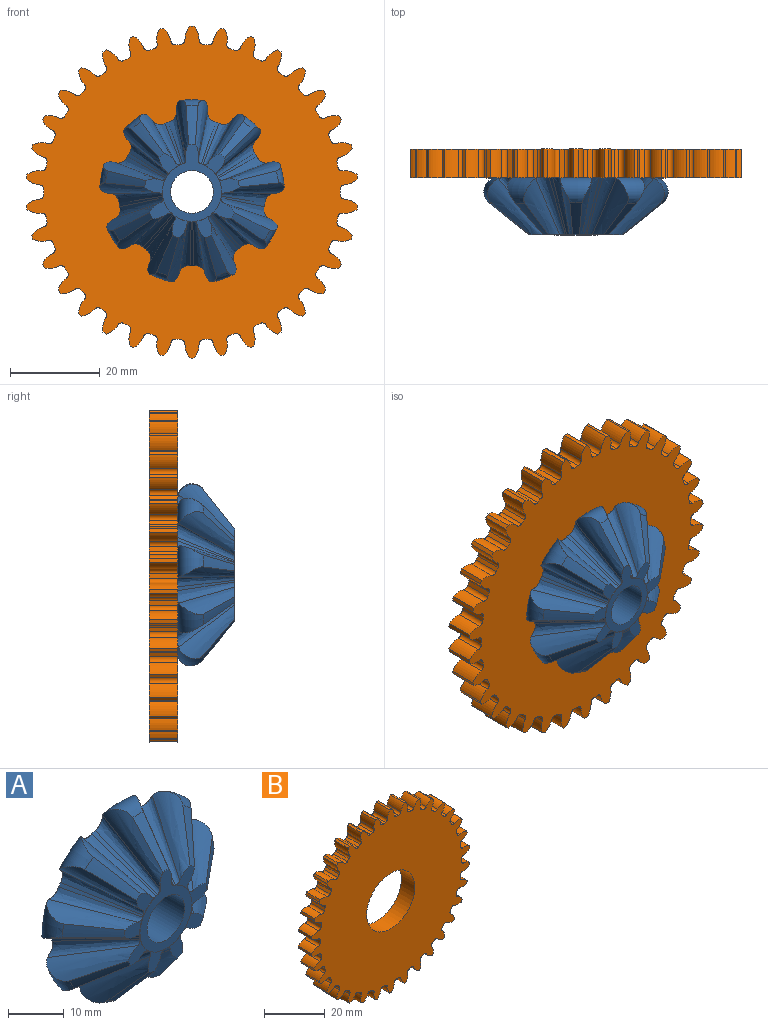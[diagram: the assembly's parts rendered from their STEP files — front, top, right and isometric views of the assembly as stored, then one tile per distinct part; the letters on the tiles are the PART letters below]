
ASSEMBLY  parts=2 mates=1
PART A: 80 faces, bbox 52.7x12.8x51.3 mm
  f0: cylinder r=6.59mm len=13.18mm, axis (0,1,0), area 3.7mm2, adj f1,f5,f6,f8,f14,f16,f17,f24
  f1: plane 17.18x13.18mm, normal (0,-1,0), area 76mm2, adj f0,f2,f3,f4,f5,f6,f79
  f2: cylinder r=4.44mm len=3.2mm, axis (0,1,0), area 0.3mm2, adj f1,f3,f6,f10
  f3: cylinder r=10.59mm len=1.48mm, axis (0,1,0), area 0.1mm2, adj f1,f2,f4,f11
  f4: cylinder r=4.44mm len=3.2mm, axis (0,1,0), area 0.3mm2, adj f1,f3,f5,f12
  f5: cylinder r=1mm len=1.11mm, axis (0,1,0), area 0.1mm2, adj f0,f1,f4,f13
  f6: cylinder r=1mm len=1.11mm, axis (0,1,0), area 0.1mm2, adj f0,f1,f2,f9
  f7: plane 34.79x34.62mm, normal (0,1,0), area 845.9mm2, adj f8,f9,f13,f14,f15,f17,f18,f22
  f8: cone r=6.59mm half-angle=37.9deg, axis (0,1,0), area 9.7mm2, adj f0,f7,f9,f22
  f9: bspline ~12.65x12.14mm, area 36.5mm2, adj f6,f7,f8,f10,f15
  f10: bspline ~18.78x12.44mm, area 59.6mm2, adj f2,f9,f11,f15
  f11: cone r=10.59mm half-angle=51.5deg, axis (0,1,0), area 23.5mm2, adj f3,f10,f12,f15
  f12: bspline ~18.78x12.44mm, area 59.6mm2, adj f4,f11,f13,f15
  f13: bspline ~12.65x12.14mm, area 36.5mm2, adj f5,f7,f12,f14,f15
  f14: cone r=6.59mm half-angle=37.9deg, axis (0,1,0), area 9.7mm2, adj f0,f7,f13,f73
  f15: torus R=17.39mm, axis (0,-1,0), area 42.8mm2, adj f7,f9,f10,f11,f12,f13
  f16: plane 5.12x4.94mm, normal (0,-1,0), area 10.8mm2, adj f0,f18,f19,f20,f21,f22
  f17: cone r=6.59mm half-angle=37.9deg, axis (0,1,0), area 9.7mm2, adj f0,f7,f18,f30
  f18: bspline ~12.65x9.08mm, area 36.5mm2, adj f7,f16,f17,f19,f23
  f19: bspline ~14.13x12.44mm, area 59.6mm2, adj f16,f18,f20,f23
  f20: cone r=10.59mm half-angle=51.5deg, axis (0,1,0), area 23.5mm2, adj f16,f19,f21,f23
  f21: bspline ~14.87x12.65mm, area 59.6mm2, adj f16,f20,f22,f23
  f22: bspline ~12.65x10.31mm, area 36.5mm2, adj f7,f8,f16,f21,f23
  f23: torus R=17.39mm, axis (0,-1,0), area 42.8mm2, adj f7,f18,f19,f20,f21,f22
  f24: plane 4.74x4.12mm, normal (0,-1,0), area 10.8mm2, adj f0,f26,f27,f28,f29,f30
  f25: cone r=6.59mm half-angle=37.9deg, axis (0,1,0), area 9.7mm2, adj f0,f7,f26,f38
  f26: bspline ~12.65x12.21mm, area 36.5mm2, adj f7,f24,f25,f27,f31
  f27: bspline ~18.84x12.65mm, area 59.6mm2, adj f24,f26,f28,f31
  f28: cone r=10.59mm half-angle=51.5deg, axis (0,1,0), area 23.5mm2, adj f24,f27,f29,f31
  f29: bspline ~18.43x12.44mm, area 59.6mm2, adj f24,f28,f30,f31
  f30: bspline ~12.65x11.71mm, area 36.5mm2, adj f7,f17,f24,f29,f31
  f31: torus R=17.39mm, axis (0,-1,0), area 42.8mm2, adj f7,f26,f27,f28,f29,f30
  f32: plane 5.15x4.62mm, normal (0,-1,0), area 10.8mm2, adj f0,f34,f35,f36,f37,f38
  f33: cone r=6.59mm half-angle=37.9deg, axis (0,1,0), area 9.7mm2, adj f0,f7,f34,f46
  f34: bspline ~12.65x9.79mm, area 36.5mm2, adj f7,f32,f33,f35,f39
  f35: bspline ~16.06x12.44mm, area 59.6mm2, adj f32,f34,f36,f39
  f36: cone r=10.59mm half-angle=51.5deg, axis (0,1,0), area 23.5mm2, adj f32,f35,f37,f39
  f37: bspline ~16.71x12.65mm, area 59.6mm2, adj f32,f36,f38,f39
  f38: bspline ~12.65x11.27mm, area 36.5mm2, adj f7,f25,f32,f37,f39
  f39: torus R=17.39mm, axis (0,-1,0), area 42.8mm2, adj f7,f34,f35,f36,f37,f38
  f40: plane 5.02x4.27mm, normal (0,-1,0), area 10.8mm2, adj f0,f42,f43,f44,f45,f46
  f41: cone r=6.59mm half-angle=37.9deg, axis (0,1,0), area 9.7mm2, adj f0,f7,f42,f54
  f42: bspline ~12.65x11.91mm, area 36.5mm2, adj f7,f40,f41,f43,f47
  f43: bspline ~17.79x12.44mm, area 59.6mm2, adj f40,f42,f44,f47
  f44: cone r=10.59mm half-angle=51.5deg, axis (0,1,0), area 23.5mm2, adj f40,f43,f45,f47
  f45: bspline ~17.76x12.65mm, area 59.6mm2, adj f40,f44,f46,f47
  f46: bspline ~12.65x10.91mm, area 36.5mm2, adj f7,f33,f40,f45,f47
  f47: torus R=17.39mm, axis (0,-1,0), area 42.8mm2, adj f7,f42,f43,f44,f45,f46
  f48: plane 5.02x4.27mm, normal (0,-1,0), area 10.8mm2, adj f0,f50,f51,f52,f53,f54
  f49: cone r=6.59mm half-angle=37.9deg, axis (0,1,0), area 9.7mm2, adj f0,f7,f50,f62
  f50: bspline ~12.65x10.91mm, area 36.5mm2, adj f7,f48,f49,f51,f55
  f51: bspline ~17.76x12.65mm, area 59.6mm2, adj f48,f50,f52,f55
  f52: cone r=10.59mm half-angle=51.5deg, axis (0,1,0), area 23.5mm2, adj f48,f51,f53,f55
  f53: bspline ~17.79x12.44mm, area 59.6mm2, adj f48,f52,f54,f55
  f54: bspline ~12.65x11.91mm, area 36.5mm2, adj f7,f41,f48,f53,f55
  f55: torus R=17.39mm, axis (0,-1,0), area 42.8mm2, adj f7,f50,f51,f52,f53,f54
  f56: plane 5.15x4.62mm, normal (0,-1,0), area 10.8mm2, adj f0,f58,f59,f60,f61,f62
  f57: cone r=6.59mm half-angle=37.9deg, axis (0,1,0), area 9.7mm2, adj f0,f7,f58,f70
  f58: bspline ~12.65x11.27mm, area 36.5mm2, adj f7,f56,f57,f59,f63
  f59: bspline ~16.71x12.65mm, area 59.6mm2, adj f56,f58,f60,f63
  f60: cone r=10.59mm half-angle=51.5deg, axis (0,1,0), area 23.5mm2, adj f56,f59,f61,f63
  f61: bspline ~16.06x12.44mm, area 59.6mm2, adj f56,f60,f62,f63
  f62: bspline ~12.65x9.79mm, area 36.5mm2, adj f7,f49,f56,f61,f63
  f63: torus R=17.39mm, axis (0,-1,0), area 42.8mm2, adj f7,f58,f59,f60,f61,f62
  f64: plane 4.74x4.12mm, normal (0,-1,0), area 10.8mm2, adj f0,f66,f67,f68,f69,f70
  f65: cone r=6.59mm half-angle=37.9deg, axis (0,1,0), area 9.7mm2, adj f0,f7,f66,f77
  f66: bspline ~12.65x11.71mm, area 36.5mm2, adj f7,f64,f65,f67,f71
  f67: bspline ~18.43x12.44mm, area 59.6mm2, adj f64,f66,f68,f71
  f68: cone r=10.59mm half-angle=51.5deg, axis (0,1,0), area 23.5mm2, adj f64,f67,f69,f71
  f69: bspline ~18.84x12.65mm, area 59.6mm2, adj f64,f68,f70,f71
  f70: bspline ~12.65x12.21mm, area 36.5mm2, adj f7,f57,f64,f69,f71
  f71: torus R=17.39mm, axis (0,-1,0), area 42.8mm2, adj f7,f66,f67,f68,f69,f70
  f72: plane 5.12x4.94mm, normal (0,-1,0), area 10.8mm2, adj f0,f73,f74,f75,f76,f77
  f73: bspline ~12.65x10.31mm, area 36.5mm2, adj f7,f14,f72,f74,f78
  f74: bspline ~14.87x12.65mm, area 59.6mm2, adj f72,f73,f75,f78
  f75: cone r=10.59mm half-angle=51.5deg, axis (0,1,0), area 23.5mm2, adj f72,f74,f76,f78
  f76: bspline ~14.13x12.44mm, area 59.6mm2, adj f72,f75,f77,f78
  f77: bspline ~12.65x9.08mm, area 36.5mm2, adj f7,f65,f72,f76,f78
  f78: torus R=17.39mm, axis (0,-1,0), area 42.8mm2, adj f7,f73,f74,f75,f76,f77
  f79: cylinder r=4.76mm len=12.75mm, axis (0,-1,0), area 381.5mm2, adj f1,f7
PART B: 207 faces, bbox 73.8x6.4x74 mm
  f0: cylinder r=33mm len=6.35mm, axis (0,1,0), area 7mm2, adj f34,f35,f40,f204
  f1: cylinder r=33mm len=6.35mm, axis (0,1,0), area 7mm2, adj f34,f35,f199,f205
  f2: cylinder r=33mm len=6.35mm, axis (0,1,0), area 7mm2, adj f34,f35,f194,f200
  f3: cylinder r=33mm len=6.35mm, axis (0,1,0), area 7mm2, adj f34,f35,f189,f195
  f4: cylinder r=33mm len=6.35mm, axis (0,1,0), area 7mm2, adj f34,f35,f184,f190
  f5: cylinder r=33mm len=6.35mm, axis (0,1,0), area 7mm2, adj f34,f35,f179,f185
  f6: cylinder r=33mm len=6.35mm, axis (0,1,0), area 7mm2, adj f34,f35,f174,f180
  f7: cylinder r=33mm len=6.35mm, axis (0,1,0), area 7mm2, adj f34,f35,f169,f175
  f8: cylinder r=33mm len=6.35mm, axis (0,1,0), area 7mm2, adj f34,f35,f164,f170
  f9: cylinder r=33mm len=6.35mm, axis (0,1,0), area 7mm2, adj f34,f35,f159,f165
  f10: cylinder r=33mm len=6.35mm, axis (0,1,0), area 7mm2, adj f34,f35,f154,f160
  f11: cylinder r=33mm len=6.35mm, axis (0,1,0), area 7mm2, adj f34,f35,f149,f155
  f12: cylinder r=33mm len=6.35mm, axis (0,1,0), area 7mm2, adj f34,f35,f144,f150
  f13: cylinder r=33mm len=6.35mm, axis (0,1,0), area 7mm2, adj f34,f35,f139,f145
  f14: cylinder r=33mm len=6.35mm, axis (0,1,0), area 7mm2, adj f34,f35,f134,f140
  f15: cylinder r=33mm len=6.35mm, axis (0,1,0), area 7mm2, adj f34,f35,f129,f135
  f16: cylinder r=33mm len=6.35mm, axis (0,1,0), area 7mm2, adj f34,f35,f124,f130
  f17: cylinder r=33mm len=6.35mm, axis (0,1,0), area 7mm2, adj f34,f35,f119,f125
  f18: cylinder r=33mm len=6.35mm, axis (0,1,0), area 7mm2, adj f34,f35,f114,f120
  f19: cylinder r=33mm len=6.35mm, axis (0,1,0), area 7mm2, adj f34,f35,f109,f115
  f20: cylinder r=33mm len=6.35mm, axis (0,1,0), area 7mm2, adj f34,f35,f104,f110
  f21: cylinder r=33mm len=6.35mm, axis (0,1,0), area 7mm2, adj f34,f35,f99,f105
  f22: cylinder r=33mm len=6.35mm, axis (0,1,0), area 7mm2, adj f34,f35,f94,f100
  f23: cylinder r=33mm len=6.35mm, axis (0,1,0), area 7mm2, adj f34,f35,f89,f95
  f24: cylinder r=33mm len=6.35mm, axis (0,1,0), area 7mm2, adj f34,f35,f84,f90
  f25: cylinder r=33mm len=6.35mm, axis (0,1,0), area 7mm2, adj f34,f35,f79,f85
  f26: cylinder r=33mm len=6.35mm, axis (0,1,0), area 7mm2, adj f34,f35,f74,f80
  f27: cylinder r=33mm len=6.35mm, axis (0,1,0), area 7mm2, adj f34,f35,f69,f75
  f28: cylinder r=33mm len=6.35mm, axis (0,1,0), area 7mm2, adj f34,f35,f64,f70
  f29: cylinder r=33mm len=6.35mm, axis (0,1,0), area 7mm2, adj f34,f35,f59,f65
  f30: cylinder r=33mm len=6.35mm, axis (0,1,0), area 7mm2, adj f34,f35,f54,f60
  f31: cylinder r=33mm len=6.35mm, axis (0,1,0), area 7mm2, adj f34,f35,f49,f55
  f32: cylinder r=33mm len=6.35mm, axis (0,1,0), area 7mm2, adj f34,f35,f44,f50
  f33: cylinder r=33mm len=6.35mm, axis (0,1,0), area 7mm2, adj f34,f35,f39,f45
  f34: plane 74x73.76mm, normal (0,-1,0), area 3393.5mm2, adj f0,f1,f2,f3,f4,f5,f6,f7
  f35: plane 74x73.76mm, normal (0,1,0), area 3393.5mm2, adj f0,f1,f2,f3,f4,f5,f6,f7
  f36: cylinder r=4.53mm len=6.35mm, axis (0,1,0), area 21.2mm2, adj f34,f35,f37,f40
  f37: cylinder r=37mm len=6.35mm, axis (0,1,0), area 5.8mm2, adj f34,f35,f36,f38
  f38: cylinder r=4.53mm len=6.35mm, axis (0,1,0), area 21.2mm2, adj f34,f35,f37,f39
  f39: cylinder r=1mm len=6.35mm, axis (0,1,0), area 9.6mm2, adj f33,f34,f35,f38
  f40: cylinder r=1mm len=6.35mm, axis (0,1,0), area 9.6mm2, adj f0,f34,f35,f36
  f41: cylinder r=4.53mm len=6.35mm, axis (0,1,0), area 21.2mm2, adj f34,f35,f42,f45
  f42: cylinder r=37mm len=6.35mm, axis (0,1,0), area 5.8mm2, adj f34,f35,f41,f43
  f43: cylinder r=4.53mm len=6.35mm, axis (0,1,0), area 21.2mm2, adj f34,f35,f42,f44
  f44: cylinder r=1mm len=6.35mm, axis (0,1,0), area 9.6mm2, adj f32,f34,f35,f43
  f45: cylinder r=1mm len=6.35mm, axis (0,1,0), area 9.6mm2, adj f33,f34,f35,f41
  f46: cylinder r=4.53mm len=6.35mm, axis (0,1,0), area 21.2mm2, adj f34,f35,f47,f50
  f47: cylinder r=37mm len=6.35mm, axis (0,1,0), area 5.8mm2, adj f34,f35,f46,f48
  f48: cylinder r=4.53mm len=6.35mm, axis (0,1,0), area 21.2mm2, adj f34,f35,f47,f49
  f49: cylinder r=1mm len=6.35mm, axis (0,1,0), area 9.6mm2, adj f31,f34,f35,f48
  f50: cylinder r=1mm len=6.35mm, axis (0,1,0), area 9.6mm2, adj f32,f34,f35,f46
  f51: cylinder r=4.53mm len=6.35mm, axis (0,1,0), area 21.2mm2, adj f34,f35,f52,f55
  f52: cylinder r=37mm len=6.35mm, axis (0,1,0), area 5.8mm2, adj f34,f35,f51,f53
  f53: cylinder r=4.53mm len=6.35mm, axis (0,1,0), area 21.2mm2, adj f34,f35,f52,f54
  f54: cylinder r=1mm len=6.35mm, axis (0,1,0), area 9.6mm2, adj f30,f34,f35,f53
  f55: cylinder r=1mm len=6.35mm, axis (0,1,0), area 9.6mm2, adj f31,f34,f35,f51
  f56: cylinder r=4.53mm len=6.35mm, axis (0,1,0), area 21.2mm2, adj f34,f35,f57,f60
  f57: cylinder r=37mm len=6.35mm, axis (0,1,0), area 5.8mm2, adj f34,f35,f56,f58
  f58: cylinder r=4.53mm len=6.35mm, axis (0,1,0), area 21.2mm2, adj f34,f35,f57,f59
  f59: cylinder r=1mm len=6.35mm, axis (0,1,0), area 9.6mm2, adj f29,f34,f35,f58
  f60: cylinder r=1mm len=6.35mm, axis (0,1,0), area 9.6mm2, adj f30,f34,f35,f56
  f61: cylinder r=4.53mm len=6.35mm, axis (0,1,0), area 21.2mm2, adj f34,f35,f62,f65
  f62: cylinder r=37mm len=6.35mm, axis (0,1,0), area 5.8mm2, adj f34,f35,f61,f63
  f63: cylinder r=4.53mm len=6.35mm, axis (0,1,0), area 21.2mm2, adj f34,f35,f62,f64
  f64: cylinder r=1mm len=6.35mm, axis (0,1,0), area 9.6mm2, adj f28,f34,f35,f63
  f65: cylinder r=1mm len=6.35mm, axis (0,1,0), area 9.6mm2, adj f29,f34,f35,f61
  f66: cylinder r=4.53mm len=6.35mm, axis (0,1,0), area 21.2mm2, adj f34,f35,f67,f70
  f67: cylinder r=37mm len=6.35mm, axis (0,1,0), area 5.8mm2, adj f34,f35,f66,f68
  f68: cylinder r=4.53mm len=6.35mm, axis (0,1,0), area 21.2mm2, adj f34,f35,f67,f69
  f69: cylinder r=1mm len=6.35mm, axis (0,1,0), area 9.6mm2, adj f27,f34,f35,f68
  f70: cylinder r=1mm len=6.35mm, axis (0,1,0), area 9.6mm2, adj f28,f34,f35,f66
  f71: cylinder r=4.53mm len=6.35mm, axis (0,1,0), area 21.2mm2, adj f34,f35,f72,f75
  f72: cylinder r=37mm len=6.35mm, axis (0,1,0), area 5.8mm2, adj f34,f35,f71,f73
  f73: cylinder r=4.53mm len=6.35mm, axis (0,1,0), area 21.2mm2, adj f34,f35,f72,f74
  f74: cylinder r=1mm len=6.35mm, axis (0,1,0), area 9.6mm2, adj f26,f34,f35,f73
  f75: cylinder r=1mm len=6.35mm, axis (0,1,0), area 9.6mm2, adj f27,f34,f35,f71
  f76: cylinder r=4.53mm len=6.35mm, axis (0,1,0), area 21.2mm2, adj f34,f35,f77,f80
  f77: cylinder r=37mm len=6.35mm, axis (0,1,0), area 5.8mm2, adj f34,f35,f76,f78
  f78: cylinder r=4.53mm len=6.35mm, axis (0,1,0), area 21.2mm2, adj f34,f35,f77,f79
  f79: cylinder r=1mm len=6.35mm, axis (0,1,0), area 9.6mm2, adj f25,f34,f35,f78
  f80: cylinder r=1mm len=6.35mm, axis (0,1,0), area 9.6mm2, adj f26,f34,f35,f76
  f81: cylinder r=4.53mm len=6.35mm, axis (0,1,0), area 21.2mm2, adj f34,f35,f82,f85
  f82: cylinder r=37mm len=6.35mm, axis (0,1,0), area 5.8mm2, adj f34,f35,f81,f83
  f83: cylinder r=4.53mm len=6.35mm, axis (0,1,0), area 21.2mm2, adj f34,f35,f82,f84
  f84: cylinder r=1mm len=6.35mm, axis (0,1,0), area 9.6mm2, adj f24,f34,f35,f83
  f85: cylinder r=1mm len=6.35mm, axis (0,1,0), area 9.6mm2, adj f25,f34,f35,f81
  f86: cylinder r=4.53mm len=6.35mm, axis (0,1,0), area 21.2mm2, adj f34,f35,f87,f90
  f87: cylinder r=37mm len=6.35mm, axis (0,1,0), area 5.8mm2, adj f34,f35,f86,f88
  f88: cylinder r=4.53mm len=6.35mm, axis (0,1,0), area 21.2mm2, adj f34,f35,f87,f89
  f89: cylinder r=1mm len=6.35mm, axis (0,1,0), area 9.6mm2, adj f23,f34,f35,f88
  f90: cylinder r=1mm len=6.35mm, axis (0,1,0), area 9.6mm2, adj f24,f34,f35,f86
  f91: cylinder r=4.53mm len=6.35mm, axis (0,1,0), area 21.2mm2, adj f34,f35,f92,f95
  f92: cylinder r=37mm len=6.35mm, axis (0,1,0), area 5.8mm2, adj f34,f35,f91,f93
  f93: cylinder r=4.53mm len=6.35mm, axis (0,1,0), area 21.2mm2, adj f34,f35,f92,f94
  f94: cylinder r=1mm len=6.35mm, axis (0,1,0), area 9.6mm2, adj f22,f34,f35,f93
  f95: cylinder r=1mm len=6.35mm, axis (0,1,0), area 9.6mm2, adj f23,f34,f35,f91
  f96: cylinder r=4.53mm len=6.35mm, axis (0,1,0), area 21.2mm2, adj f34,f35,f97,f100
  f97: cylinder r=37mm len=6.35mm, axis (0,1,0), area 5.8mm2, adj f34,f35,f96,f98
  f98: cylinder r=4.53mm len=6.35mm, axis (0,1,0), area 21.2mm2, adj f34,f35,f97,f99
  f99: cylinder r=1mm len=6.35mm, axis (0,1,0), area 9.6mm2, adj f21,f34,f35,f98
  f100: cylinder r=1mm len=6.35mm, axis (0,1,0), area 9.6mm2, adj f22,f34,f35,f96
  f101: cylinder r=4.53mm len=6.35mm, axis (0,1,0), area 21.2mm2, adj f34,f35,f102,f105
  f102: cylinder r=37mm len=6.35mm, axis (0,1,0), area 5.8mm2, adj f34,f35,f101,f103
  f103: cylinder r=4.53mm len=6.35mm, axis (0,1,0), area 21.2mm2, adj f34,f35,f102,f104
  f104: cylinder r=1mm len=6.35mm, axis (0,1,0), area 9.6mm2, adj f20,f34,f35,f103
  f105: cylinder r=1mm len=6.35mm, axis (0,1,0), area 9.6mm2, adj f21,f34,f35,f101
  f106: cylinder r=4.53mm len=6.35mm, axis (0,1,0), area 21.2mm2, adj f34,f35,f107,f110
  f107: cylinder r=37mm len=6.35mm, axis (0,1,0), area 5.8mm2, adj f34,f35,f106,f108
  f108: cylinder r=4.53mm len=6.35mm, axis (0,1,0), area 21.2mm2, adj f34,f35,f107,f109
  f109: cylinder r=1mm len=6.35mm, axis (0,1,0), area 9.6mm2, adj f19,f34,f35,f108
  f110: cylinder r=1mm len=6.35mm, axis (0,1,0), area 9.6mm2, adj f20,f34,f35,f106
  f111: cylinder r=4.53mm len=6.35mm, axis (0,1,0), area 21.2mm2, adj f34,f35,f112,f115
  f112: cylinder r=37mm len=6.35mm, axis (0,1,0), area 5.8mm2, adj f34,f35,f111,f113
  f113: cylinder r=4.53mm len=6.35mm, axis (0,1,0), area 21.2mm2, adj f34,f35,f112,f114
  f114: cylinder r=1mm len=6.35mm, axis (0,1,0), area 9.6mm2, adj f18,f34,f35,f113
  f115: cylinder r=1mm len=6.35mm, axis (0,1,0), area 9.6mm2, adj f19,f34,f35,f111
  f116: cylinder r=4.53mm len=6.35mm, axis (0,1,0), area 21.2mm2, adj f34,f35,f117,f120
  f117: cylinder r=37mm len=6.35mm, axis (0,1,0), area 5.8mm2, adj f34,f35,f116,f118
  f118: cylinder r=4.53mm len=6.35mm, axis (0,1,0), area 21.2mm2, adj f34,f35,f117,f119
  f119: cylinder r=1mm len=6.35mm, axis (0,1,0), area 9.6mm2, adj f17,f34,f35,f118
  f120: cylinder r=1mm len=6.35mm, axis (0,1,0), area 9.6mm2, adj f18,f34,f35,f116
  f121: cylinder r=4.53mm len=6.35mm, axis (0,1,0), area 21.2mm2, adj f34,f35,f122,f125
  f122: cylinder r=37mm len=6.35mm, axis (0,1,0), area 5.8mm2, adj f34,f35,f121,f123
  f123: cylinder r=4.53mm len=6.35mm, axis (0,1,0), area 21.2mm2, adj f34,f35,f122,f124
  f124: cylinder r=1mm len=6.35mm, axis (0,1,0), area 9.6mm2, adj f16,f34,f35,f123
  f125: cylinder r=1mm len=6.35mm, axis (0,1,0), area 9.6mm2, adj f17,f34,f35,f121
  f126: cylinder r=4.53mm len=6.35mm, axis (0,1,0), area 21.2mm2, adj f34,f35,f127,f130
  f127: cylinder r=37mm len=6.35mm, axis (0,1,0), area 5.8mm2, adj f34,f35,f126,f128
  f128: cylinder r=4.53mm len=6.35mm, axis (0,1,0), area 21.2mm2, adj f34,f35,f127,f129
  f129: cylinder r=1mm len=6.35mm, axis (0,1,0), area 9.6mm2, adj f15,f34,f35,f128
  f130: cylinder r=1mm len=6.35mm, axis (0,1,0), area 9.6mm2, adj f16,f34,f35,f126
  f131: cylinder r=4.53mm len=6.35mm, axis (0,1,0), area 21.2mm2, adj f34,f35,f132,f135
  f132: cylinder r=37mm len=6.35mm, axis (0,1,0), area 5.8mm2, adj f34,f35,f131,f133
  f133: cylinder r=4.53mm len=6.35mm, axis (0,1,0), area 21.2mm2, adj f34,f35,f132,f134
  f134: cylinder r=1mm len=6.35mm, axis (0,1,0), area 9.6mm2, adj f14,f34,f35,f133
  f135: cylinder r=1mm len=6.35mm, axis (0,1,0), area 9.6mm2, adj f15,f34,f35,f131
  f136: cylinder r=4.53mm len=6.35mm, axis (0,1,0), area 21.2mm2, adj f34,f35,f137,f140
  f137: cylinder r=37mm len=6.35mm, axis (0,1,0), area 5.8mm2, adj f34,f35,f136,f138
  f138: cylinder r=4.53mm len=6.35mm, axis (0,1,0), area 21.2mm2, adj f34,f35,f137,f139
  f139: cylinder r=1mm len=6.35mm, axis (0,1,0), area 9.6mm2, adj f13,f34,f35,f138
  f140: cylinder r=1mm len=6.35mm, axis (0,1,0), area 9.6mm2, adj f14,f34,f35,f136
  f141: cylinder r=4.53mm len=6.35mm, axis (0,1,0), area 21.2mm2, adj f34,f35,f142,f145
  f142: cylinder r=37mm len=6.35mm, axis (0,1,0), area 5.8mm2, adj f34,f35,f141,f143
  f143: cylinder r=4.53mm len=6.35mm, axis (0,1,0), area 21.2mm2, adj f34,f35,f142,f144
  f144: cylinder r=1mm len=6.35mm, axis (0,1,0), area 9.6mm2, adj f12,f34,f35,f143
  f145: cylinder r=1mm len=6.35mm, axis (0,1,0), area 9.6mm2, adj f13,f34,f35,f141
  f146: cylinder r=4.53mm len=6.35mm, axis (0,1,0), area 21.2mm2, adj f34,f35,f147,f150
  f147: cylinder r=37mm len=6.35mm, axis (0,1,0), area 5.8mm2, adj f34,f35,f146,f148
  f148: cylinder r=4.53mm len=6.35mm, axis (0,1,0), area 21.2mm2, adj f34,f35,f147,f149
  f149: cylinder r=1mm len=6.35mm, axis (0,1,0), area 9.6mm2, adj f11,f34,f35,f148
  f150: cylinder r=1mm len=6.35mm, axis (0,1,0), area 9.6mm2, adj f12,f34,f35,f146
  f151: cylinder r=4.53mm len=6.35mm, axis (0,1,0), area 21.2mm2, adj f34,f35,f152,f155
  f152: cylinder r=37mm len=6.35mm, axis (0,1,0), area 5.8mm2, adj f34,f35,f151,f153
  f153: cylinder r=4.53mm len=6.35mm, axis (0,1,0), area 21.2mm2, adj f34,f35,f152,f154
  f154: cylinder r=1mm len=6.35mm, axis (0,1,0), area 9.6mm2, adj f10,f34,f35,f153
  f155: cylinder r=1mm len=6.35mm, axis (0,1,0), area 9.6mm2, adj f11,f34,f35,f151
  f156: cylinder r=4.53mm len=6.35mm, axis (0,1,0), area 21.2mm2, adj f34,f35,f157,f160
  f157: cylinder r=37mm len=6.35mm, axis (0,1,0), area 5.8mm2, adj f34,f35,f156,f158
  f158: cylinder r=4.53mm len=6.35mm, axis (0,1,0), area 21.2mm2, adj f34,f35,f157,f159
  f159: cylinder r=1mm len=6.35mm, axis (0,1,0), area 9.6mm2, adj f9,f34,f35,f158
  f160: cylinder r=1mm len=6.35mm, axis (0,1,0), area 9.6mm2, adj f10,f34,f35,f156
  f161: cylinder r=4.53mm len=6.35mm, axis (0,1,0), area 21.2mm2, adj f34,f35,f162,f165
  f162: cylinder r=37mm len=6.35mm, axis (0,1,0), area 5.8mm2, adj f34,f35,f161,f163
  f163: cylinder r=4.53mm len=6.35mm, axis (0,1,0), area 21.2mm2, adj f34,f35,f162,f164
  f164: cylinder r=1mm len=6.35mm, axis (0,1,0), area 9.6mm2, adj f8,f34,f35,f163
  f165: cylinder r=1mm len=6.35mm, axis (0,1,0), area 9.6mm2, adj f9,f34,f35,f161
  f166: cylinder r=4.53mm len=6.35mm, axis (0,1,0), area 21.2mm2, adj f34,f35,f167,f170
  f167: cylinder r=37mm len=6.35mm, axis (0,1,0), area 5.8mm2, adj f34,f35,f166,f168
  f168: cylinder r=4.53mm len=6.35mm, axis (0,1,0), area 21.2mm2, adj f34,f35,f167,f169
  f169: cylinder r=1mm len=6.35mm, axis (0,1,0), area 9.6mm2, adj f7,f34,f35,f168
  f170: cylinder r=1mm len=6.35mm, axis (0,1,0), area 9.6mm2, adj f8,f34,f35,f166
  f171: cylinder r=4.53mm len=6.35mm, axis (0,1,0), area 21.2mm2, adj f34,f35,f172,f175
  f172: cylinder r=37mm len=6.35mm, axis (0,1,0), area 5.8mm2, adj f34,f35,f171,f173
  f173: cylinder r=4.53mm len=6.35mm, axis (0,1,0), area 21.2mm2, adj f34,f35,f172,f174
  f174: cylinder r=1mm len=6.35mm, axis (0,1,0), area 9.6mm2, adj f6,f34,f35,f173
  f175: cylinder r=1mm len=6.35mm, axis (0,1,0), area 9.6mm2, adj f7,f34,f35,f171
  f176: cylinder r=4.53mm len=6.35mm, axis (0,1,0), area 21.2mm2, adj f34,f35,f177,f180
  f177: cylinder r=37mm len=6.35mm, axis (0,1,0), area 5.8mm2, adj f34,f35,f176,f178
  f178: cylinder r=4.53mm len=6.35mm, axis (0,1,0), area 21.2mm2, adj f34,f35,f177,f179
  f179: cylinder r=1mm len=6.35mm, axis (0,1,0), area 9.6mm2, adj f5,f34,f35,f178
  f180: cylinder r=1mm len=6.35mm, axis (0,1,0), area 9.6mm2, adj f6,f34,f35,f176
  f181: cylinder r=4.53mm len=6.35mm, axis (0,1,0), area 21.2mm2, adj f34,f35,f182,f185
  f182: cylinder r=37mm len=6.35mm, axis (0,1,0), area 5.8mm2, adj f34,f35,f181,f183
  f183: cylinder r=4.53mm len=6.35mm, axis (0,1,0), area 21.2mm2, adj f34,f35,f182,f184
  f184: cylinder r=1mm len=6.35mm, axis (0,1,0), area 9.6mm2, adj f4,f34,f35,f183
  f185: cylinder r=1mm len=6.35mm, axis (0,1,0), area 9.6mm2, adj f5,f34,f35,f181
  f186: cylinder r=4.53mm len=6.35mm, axis (0,1,0), area 21.2mm2, adj f34,f35,f187,f190
  f187: cylinder r=37mm len=6.35mm, axis (0,1,0), area 5.8mm2, adj f34,f35,f186,f188
  f188: cylinder r=4.53mm len=6.35mm, axis (0,1,0), area 21.2mm2, adj f34,f35,f187,f189
  f189: cylinder r=1mm len=6.35mm, axis (0,1,0), area 9.6mm2, adj f3,f34,f35,f188
  f190: cylinder r=1mm len=6.35mm, axis (0,1,0), area 9.6mm2, adj f4,f34,f35,f186
  f191: cylinder r=4.53mm len=6.35mm, axis (0,1,0), area 21.2mm2, adj f34,f35,f192,f195
  f192: cylinder r=37mm len=6.35mm, axis (0,1,0), area 5.8mm2, adj f34,f35,f191,f193
  f193: cylinder r=4.53mm len=6.35mm, axis (0,1,0), area 21.2mm2, adj f34,f35,f192,f194
  f194: cylinder r=1mm len=6.35mm, axis (0,1,0), area 9.6mm2, adj f2,f34,f35,f193
  f195: cylinder r=1mm len=6.35mm, axis (0,1,0), area 9.6mm2, adj f3,f34,f35,f191
  f196: cylinder r=4.53mm len=6.35mm, axis (0,1,0), area 21.2mm2, adj f34,f35,f197,f200
  f197: cylinder r=37mm len=6.35mm, axis (0,1,0), area 5.8mm2, adj f34,f35,f196,f198
  f198: cylinder r=4.53mm len=6.35mm, axis (0,1,0), area 21.2mm2, adj f34,f35,f197,f199
  f199: cylinder r=1mm len=6.35mm, axis (0,1,0), area 9.6mm2, adj f1,f34,f35,f198
  f200: cylinder r=1mm len=6.35mm, axis (0,1,0), area 9.6mm2, adj f2,f34,f35,f196
  f201: cylinder r=4.53mm len=6.35mm, axis (0,1,0), area 21.2mm2, adj f34,f35,f202,f205
  f202: cylinder r=37mm len=6.35mm, axis (0,1,0), area 5.8mm2, adj f34,f35,f201,f203
  f203: cylinder r=4.53mm len=6.35mm, axis (0,1,0), area 21.2mm2, adj f34,f35,f202,f204
  f204: cylinder r=1mm len=6.35mm, axis (0,1,0), area 9.6mm2, adj f0,f34,f35,f203
  f205: cylinder r=1mm len=6.35mm, axis (0,1,0), area 9.6mm2, adj f1,f34,f35,f201
  f206: cylinder r=11.24mm len=22.48mm, axis (0,-1,0), area 448.4mm2, adj f34,f35
PLACE A at identity fixed
PLACE B t=(0,15.88,0)mm
MATE fastened A.f79 <-> B.f0  axis (0,-1,0) through (0,12.7,0)mm
